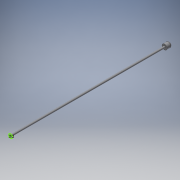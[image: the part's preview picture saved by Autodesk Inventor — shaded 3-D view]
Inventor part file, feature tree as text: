
AUTODESK INVENTOR PART (.ipt)
format: ipt  version: 2018 (Build 220112000, 112)  size: 110,080 bytes
history: native  units: in
note: dims shown in document units (in); Inventor stores cm internally (conversion verified against a paired STEP export)
features: sketch x5, extrude x3, plane x1, fillet x1
ambient origin geometry x8: Origin, YZ Plane, XZ Plane, XY Plane, X Axis, Y Axis, Z Axis, Center Point
bodies: Solid1 (feature_tree)
feature tree (10):
  sketch  "Sketch1"  dims[d0=59.0551in d1=0.3937in d2=0.0in]
  sketch  "Sketch2"  dims[d3=157.4803in d4=157.4803in d5=0.0in d6=39.3701in]
  plane  "Work Plane1"
  extrude  "Extrusion1"  Depth=0.3937in TaperAngle=0.0deg
  extrude  "Extrusion2"  Depth=157.4803in TaperAngle=0.0deg
  fillet  "Fillet1"  Radius=39.3701in
  extrude  "Extrusion3"  Depth=157.4803in TaperAngle=0.0deg
  sketch  "Sketch5"
  sketch  "Sketch3"  dims[d7=31.4961in d8=157.4803in d9=0.0in]
  sketch  "Sketch4"  dims[d10=125.9843in]
